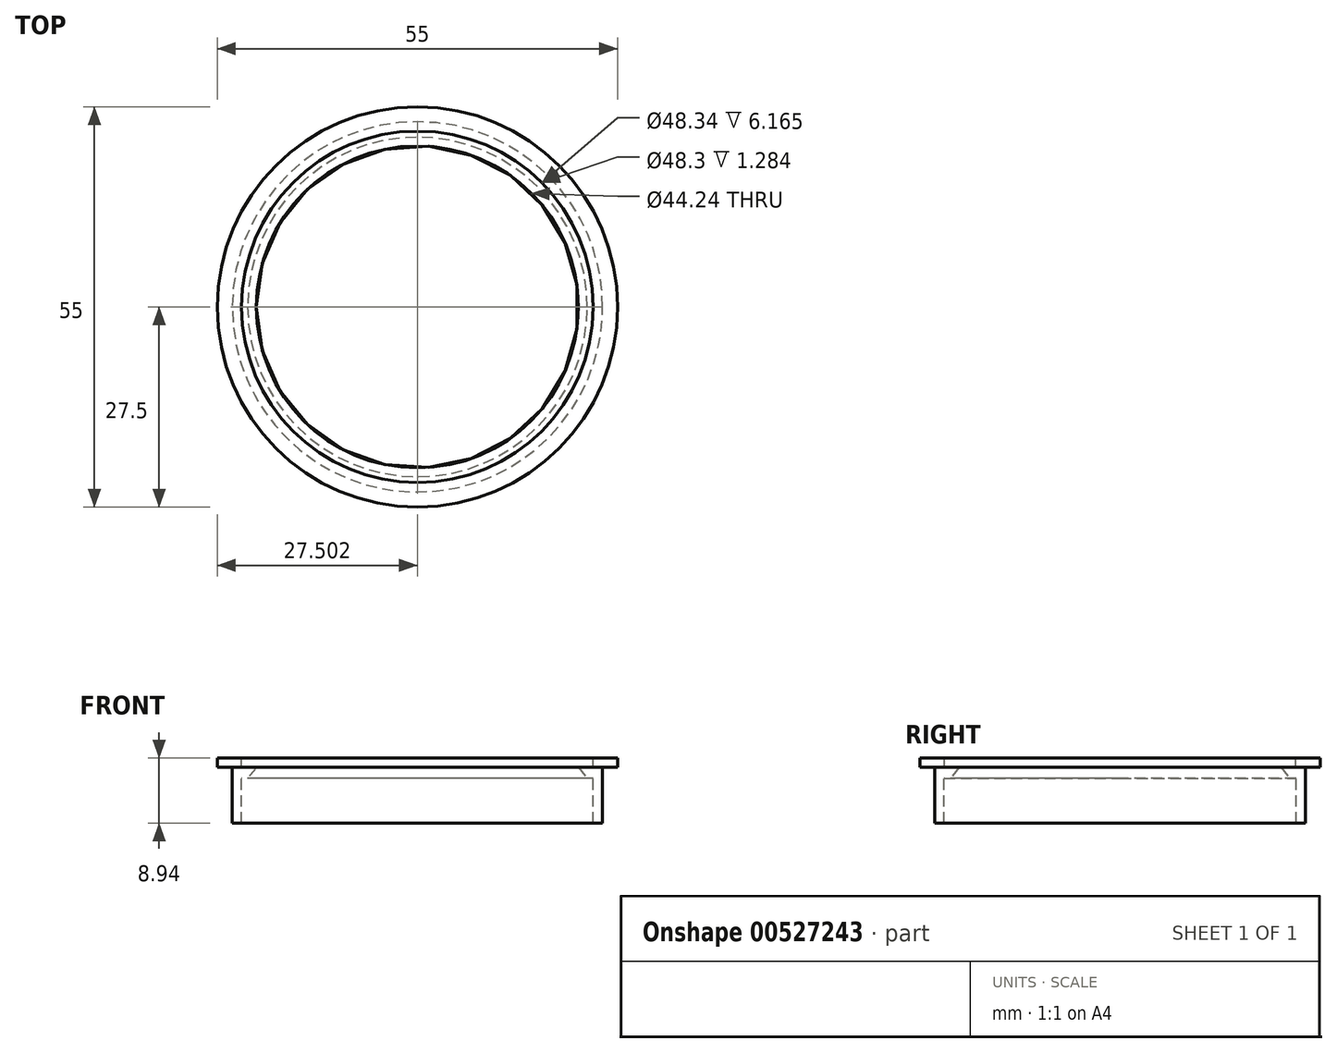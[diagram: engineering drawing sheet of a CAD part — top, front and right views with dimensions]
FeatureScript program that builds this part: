
annotation { "Feature Type Name" : "Feature", "Feature Type Description" : "" }
export const myFeature = defineFeature(function(context is Context, id is Id, definition is map)
    precondition{}
    {
        {
            var Q0;
            Q0=qCreatedBy(makeId("Front.planeOp"),FACE);
            var sketch = newSketch(context, id + "F0", { "sketchPlane" : qUnion([Q0])});
            skLineSegment(sketch, "E0.bottom", {"start": v(-11.52, 15.14) * mm, "end": v(-10.25, 15.14) * mm});
            skLineSegment(sketch, "E0.top", {"start": v(-11.54, 7.48) * mm, "end": v(-10.27, 7.48) * mm});
            skLineSegment(sketch, "E0.left", {"start": v(-11.54, 15.15) * mm, "end": v(-11.54, 7.48) * mm});
            skLineSegment(sketch, "E0.right", {"start": v(-10.27, 15.15) * mm, "end": v(-10.27, 7.48) * mm});
            skLineSegment(sketch, "E1.bottom", {"start": v(-13.6, 16.42) * mm, "end": v(-10.27, 16.42) * mm});
            skLineSegment(sketch, "E1.top", {"start": v(-13.6, 15.14) * mm, "end": v(-10.27, 15.14) * mm});
            skLineSegment(sketch, "E1.left", {"start": v(-13.6, 16.42) * mm, "end": v(-13.6, 15.14) * mm});
            skLineSegment(sketch, "E1.right", {"start": v(-10.27, 16.42) * mm, "end": v(-10.27, 15.17) * mm});
            skLineSegment(sketch, "E2", {"start": v(-8.22, 15.14) * mm, "end": v(-7.54, 11.58) * mm});
            skLineSegment(sketch, "E3", {"start": v(-7.54, 11.58) * mm, "end": v(-8.46, 11.58) * mm});
            skLineSegment(sketch, "E4", {"start": v(-8.46, 11.58) * mm, "end": v(-9.43, 13.65) * mm});
            skLineSegment(sketch, "E5", {"start": v(13.9, 22.36) * mm, "end": v(13.9, -4.12) * mm});
            skLineSegment(sketch, "E6", {"start": v(-9.43, 13.65) * mm, "end": v(-8.22, 15.14) * mm});
            skLineSegment(sketch, "E7.bottom", {"start": v(-8.22, 13.65) * mm, "end": v(-11.52, 13.65) * mm});
            skLineSegment(sketch, "E7.top", {"start": v(-8.22, 15.14) * mm, "end": v(-11.52, 15.14) * mm});
            skLineSegment(sketch, "E7.left", {"start": v(-8.22, 13.65) * mm, "end": v(-8.22, 15.14) * mm});
            skLineSegment(sketch, "E7.right", {"start": v(-11.52, 13.65) * mm, "end": v(-11.52, 15.14) * mm});
            skLineSegment(sketch, "E8.bottom", {"start": v(-13.6, 16.42) * mm, "end": v(-10.25, 16.42) * mm});
            skLineSegment(sketch, "E8.top", {"start": v(-13.6, 15.14) * mm, "end": v(-10.25, 15.14) * mm});
            skLineSegment(sketch, "E8.right", {"start": v(-10.25, 16.42) * mm, "end": v(-10.25, 15.14) * mm});
            skLineSegment(sketch, "E9.bottom", {"start": v(-11.52, 13.65) * mm, "end": v(-8.22, 13.65) * mm});
            skLineSegment(sketch, "E9.top", {"start": v(-11.52, 15.14) * mm, "end": v(-8.22, 15.14) * mm});
            skLineSegment(sketch, "E10.top", {"start": v(-8.46, 11.58) * mm, "end": v(-7.54, 11.58) * mm});
            skLineSegment(sketch, "E10.left", {"start": v(-9.43, 13.65) * mm, "end": v(-8.46, 11.58) * mm});
            skSolve(sketch);
        }
        {
            var Q0;
            {var subQ5=sQuery(id+"F0.wireOp",EDGE,"E8.right");Q0=makeQuery(id+"F0.imprint","IMPRINT",FACE,{"disambiguationData":[TD([[makeQuery(id+"F0.imprint","IMPRINT",EDGE,{"derivedFrom":subQ5}),-1.0]])]});}
            var Q1;
            {var subQ1=sQuery(id+"F0.wireOp",EDGE,"E10.top");Q1=makeQuery(id+"F0.imprint","IMPRINT",FACE,{"disambiguationData":[TD([[makeQuery(id+"F0.imprint","IMPRINT",EDGE,{"derivedFrom":subQ1}),1.0]])]});}
            var Q2;
            {var subQ1=sQuery(id+"F0.wireOp",EDGE,"E9.bottom");var subQ3=sQuery(id+"F0.wireOp",EDGE,"E7.left");var subQ4=makeQuery(id+"F0.imprint","INTERSECT",VERTEX,{"derivedFrom":[subQ1,subQ3]});Q2=makeQuery(id+"F0.imprint","IMPRINT",FACE,{"disambiguationData":[TD([[makeQuery(id+"F0.imprint","IMPRINT",EDGE,{"disambiguationData":[TD([[subQ4,-1.0]])],"derivedFrom":subQ3}),1.0]])]});}
            var Q3;
            {var subQ5=sQuery(id+"F0.wireOp",EDGE,"E7.right");Q3=makeQuery(id+"F0.imprint","IMPRINT",FACE,{"disambiguationData":[TD([[makeQuery(id+"F0.imprint","IMPRINT",EDGE,{"derivedFrom":subQ5}),-1.0]])]});}
            var Q4;
            {var subQ2=sQuery(id+"F0.wireOp",EDGE,"E6");Q4=makeQuery(id+"F0.imprint","IMPRINT",FACE,{"disambiguationData":[TD([[makeQuery(id+"F0.imprint","IMPRINT",EDGE,{"derivedFrom":subQ2}),1.0]])]});}
            var Q5;
            {var subQ4=sQuery(id+"F0.wireOp",EDGE,"E0.top");Q5=makeQuery(id+"F0.imprint","IMPRINT",FACE,{"disambiguationData":[TD([[makeQuery(id+"F0.imprint","IMPRINT",EDGE,{"derivedFrom":subQ4}),1.0]])]});}
            var Q6;
            Q6=sQuery(id+"F0.wireOp",EDGE,"E5");
            revolve(context, id + "F1", {"entities" : qUnion([Q0, Q1, Q2, Q3, Q4, Q5]), "axis" : qUnion([Q6]), "revolveType" : RevolveType.FULL});
        }
    });
